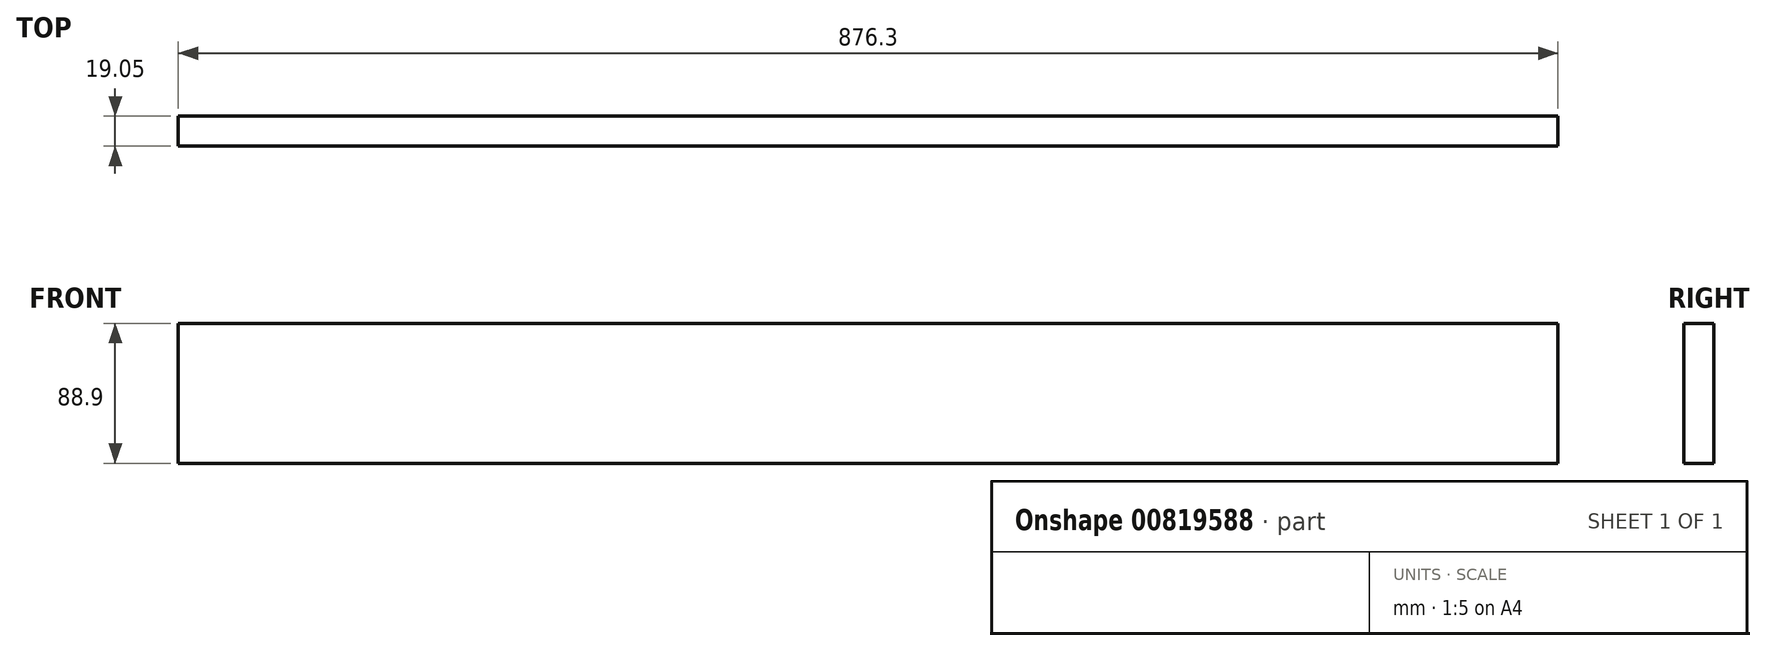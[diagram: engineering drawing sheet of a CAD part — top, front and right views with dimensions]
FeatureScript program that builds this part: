
annotation { "Feature Type Name" : "Feature", "Feature Type Description" : "" }
export const myFeature = defineFeature(function(context is Context, id is Id, definition is map)
    precondition{}
    {
        {
            var Q0;
            Q0=qCreatedBy(makeId("Front.planeOp"),FACE);
            var sketch = newSketch(context, id + "F0", { "sketchPlane" : qUnion([Q0])});
            skLineSegment(sketch, "E0.bottom", {"start": v(438.15, 44.45) * mm, "end": v(-438.15, 44.45) * mm});
            skLineSegment(sketch, "E0.top", {"start": v(438.15, -44.45) * mm, "end": v(-438.15, -44.45) * mm});
            skLineSegment(sketch, "E0.left", {"start": v(438.15, 44.45) * mm, "end": v(438.15, -44.45) * mm});
            skLineSegment(sketch, "E0.right", {"start": v(-438.15, 44.45) * mm, "end": v(-438.15, -44.45) * mm});
            skPoint(sketch, "E0.middle", {"position": v(0, 0) * mm});
            skSolve(sketch);
        }
        {
            var Q0;
            Q0=makeQuery(id+"F0.imprint","IMPRINT",FACE,{"disambiguationData":[TD([[makeQuery(id+"F0.imprint","IMPRINT",EDGE,{"derivedFrom":sQuery(id+"F0.wireOp",EDGE,"E0.bottom")}),1.0]])]});
            extrude(context, id + "F1", {"entities" : qUnion([Q0]), "depth" : 19.05 * mm, "offsetDistance" : 25.4 * mm});
        }
        {
            var Q0;
            Q0=makeQuery(id+"F1.opExtrude","SWEPT_BODY",BODY,{"disambiguationData":[OSD([sQuery(id+"F0.wireOp",EDGE,"E0.bottom"),sQuery(id+"F0.wireOp",EDGE,"E0.top"),sQuery(id+"F0.wireOp",EDGE,"E0.left"),sQuery(id+"F0.wireOp",EDGE,"E0.right")])]});
            transform(context, id + "F2", {"entities" : qUnion([Q0]), "transformType" : TransformType.TRANSLATION_3D, "dx" : 0 * mm, "dy" : 0 * mm, "dz" : 0 * mm, "makeCopy" : true});
        }
        {
            var Q0;
            Q0=makeQuery(id+"F2.opPattern","COPY",BODY,{"derivedFrom":makeQuery(id+"F1.opExtrude","SWEPT_BODY",BODY,{"disambiguationData":[OSD([sQuery(id+"F0.wireOp",EDGE,"E0.bottom"),sQuery(id+"F0.wireOp",EDGE,"E0.top"),sQuery(id+"F0.wireOp",EDGE,"E0.left"),sQuery(id+"F0.wireOp",EDGE,"E0.right")])]}),"instanceName":"1"});
            deleteBodies(context, id + "F3", {"entities" : qUnion([Q0])});
        }
    });
